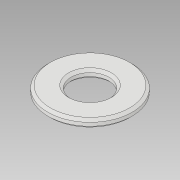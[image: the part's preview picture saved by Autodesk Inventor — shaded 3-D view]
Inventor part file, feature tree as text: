
AUTODESK INVENTOR PART (.ipt)
format: ipt  version: 2019 (Build 230136000, 136)  size: 97,280 bytes
history: native  units: mm
features: other x1, extrude x1, chamfer x1, sketch x1
ambient origin geometry x8: Origin, YZ Plane, XZ Plane, XY Plane, X Axis, Y Axis, Z Axis, Center Point
bodies: Body1 (feature_tree)
feature tree (4):
  other  "Sólido1"
  extrude  "Extrusión1"  Depth=1.0mm
  chamfer  "Chaflán1"  Distance=1.0mm
  sketch  "Boceto1"  dims[d0=10.0mm d1=4.5mm d2=1.0mm d3=0.0mm d4=0.3mm d5=2.0mm d6=45.0deg]
